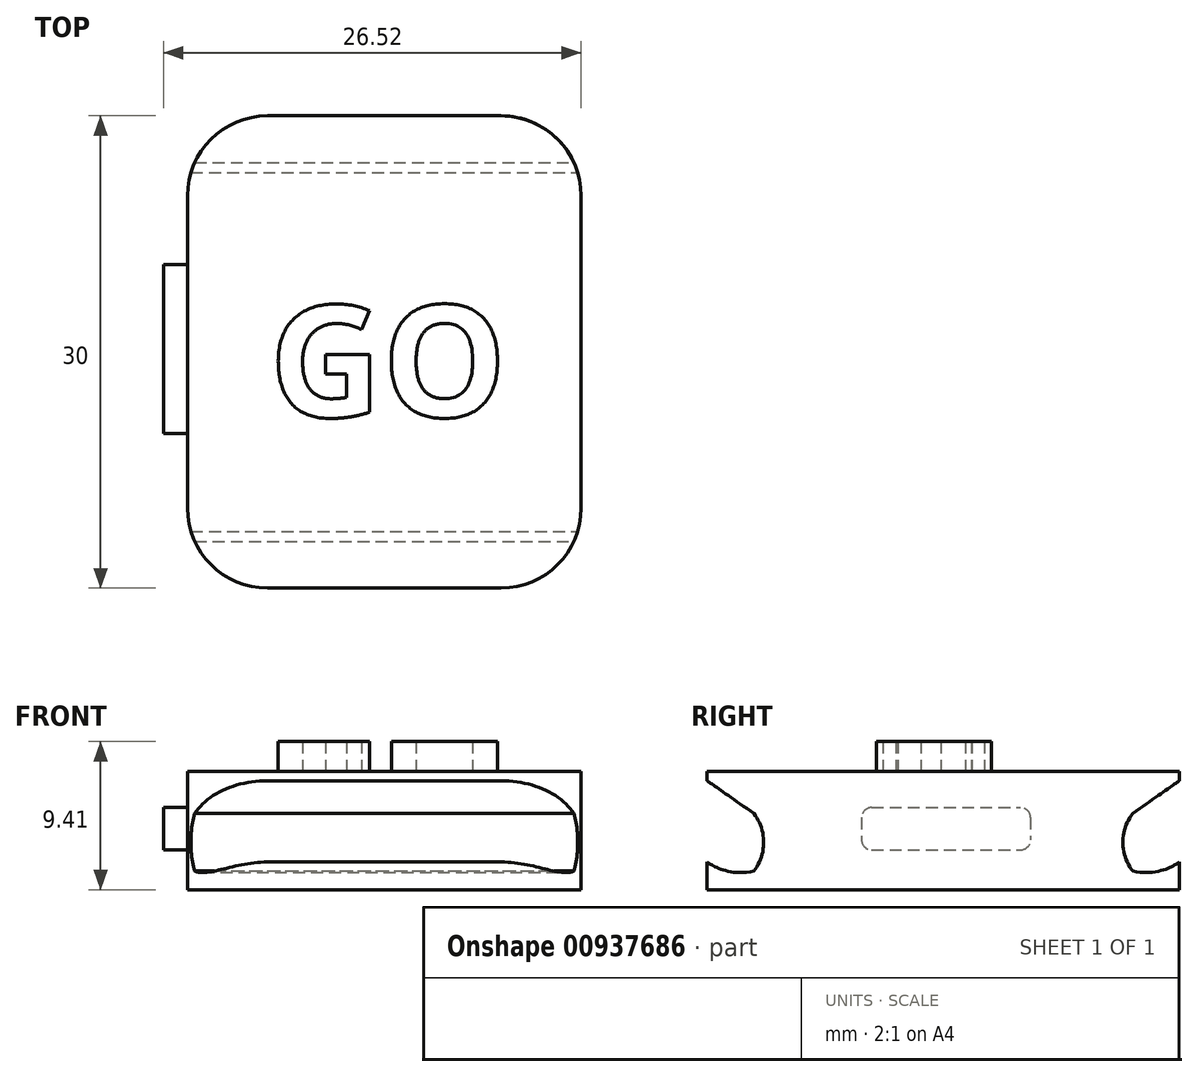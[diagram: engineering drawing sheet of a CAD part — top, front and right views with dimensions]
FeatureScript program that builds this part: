
annotation { "Feature Type Name" : "Feature", "Feature Type Description" : "" }
export const myFeature = defineFeature(function(context is Context, id is Id, definition is map)
    precondition{}
    {
        {
            var Q0;
            Q0=qCreatedBy(makeId("Top.planeOp"),FACE);
            var sketch = newSketch(context, id + "F0", { "sketchPlane" : qUnion([Q0])});
            skLineSegment(sketch, "E0.bottom", {"start": v(0, 0) * mm, "end": v(25, 0) * mm});
            skLineSegment(sketch, "E0.top", {"start": v(0, 30) * mm, "end": v(25, 30) * mm});
            skLineSegment(sketch, "E0.left", {"start": v(0, 0) * mm, "end": v(0, 30) * mm});
            skLineSegment(sketch, "E0.right", {"start": v(25, 0) * mm, "end": v(25, 30) * mm});
            skSolve(sketch);
        }
        {
            var Q0;
            Q0=makeQuery(id+"F0.imprint","IMPRINT",FACE,{"disambiguationData":[TD([[makeQuery(id+"F0.imprint","IMPRINT",EDGE,{"derivedFrom":sQuery(id+"F0.wireOp",EDGE,"E0.bottom")}),1.0]])]});
            extrude(context, id + "F1", {"entities" : qUnion([Q0]), "depth" : 7.5 * mm, "offsetDistance" : 25.4 * mm});
        }
        {
            var Q0;
            Q0=makeQuery(id+"F1.opExtrude","SWEPT_FACE",FACE,{"disambiguationData":[OSD([sQuery(id+"F0.wireOp",EDGE,"E0.right")])]});
            var sketch = newSketch(context, id + "F2", { "sketchPlane" : qUnion([Q0])});
            skArc(sketch, "E1", {"start": v(0, 1.76) * mm, "mid": v(1.42, 1.16) * mm, "end": v(2.97, 1.19) * mm});
            skArc(sketch, "E2", {"start": v(2.97, 1.19) * mm, "mid": v(3.6, 3.02) * mm, "end": v(2.97, 4.84) * mm});
            skLineSegment(sketch, "E3", {"start": v(2.97, 4.84) * mm, "end": v(0, 6.92) * mm});
            skLineSegment(sketch, "E4", {"start": v(15, 7.5) * mm, "end": v(15, 0) * mm, "construction": true});
            skLineSegment(sketch, "E5.MirrorCS", {"start": v(27.03, 4.84) * mm, "end": v(30, 6.92) * mm});
            skArc(sketch, "E6.MirrorCS", {"start": v(27.03, 1.19) * mm, "mid": v(26.4, 3.02) * mm, "end": v(27.03, 4.84) * mm});
            skArc(sketch, "E7.MirrorCS", {"start": v(30, 1.76) * mm, "mid": v(28.58, 1.16) * mm, "end": v(27.03, 1.19) * mm});
            skLineSegment(sketch, "E8", {"start": v(0, 6.92) * mm, "end": v(0, 1.76) * mm});
            skLineSegment(sketch, "E9", {"start": v(30, 6.92) * mm, "end": v(30, 1.76) * mm});
            skSolve(sketch);
        }
        {
            var Q0;
            Q0 = qSketchRegion(id + "F2", true);
            extrude(context, id + "F3", {"entities" : qUnion([Q0]), "operationType" : NewBodyOperationType.REMOVE, "oppositeDirection" : true, "depth" : 25.4 * mm, "offsetDistance" : 25.4 * mm});
        }
        {
            var Q0;
            {var subQ0=sQuery(id+"F0.wireOp",EDGE,"E0.bottom");var subQ1=sQuery(id+"F0.wireOp",EDGE,"E0.right");Q0=makeQuery(id+"F3.boolean.opBoolean","SPLIT",EDGE,{"disambiguationData":[TD([makeQuery(id+"F3.opExtrude","SWEPT_FACE",FACE,{"disambiguationData":[OSD([sQuery(id+"F2.wireOp",EDGE,"E3")])]})])],"derivedFrom":makeQuery(id+"F1.opExtrude","SWEPT_EDGE",EDGE,{"disambiguationData":[OSD([subQ0,subQ1])]})});}
            var Q1;
            {var subQ0=sQuery(id+"F0.wireOp",EDGE,"E0.bottom");var subQ1=sQuery(id+"F0.wireOp",EDGE,"E0.left");Q1=makeQuery(id+"F3.boolean.opBoolean","SPLIT",EDGE,{"disambiguationData":[TD([makeQuery(id+"F3.opExtrude","SWEPT_FACE",FACE,{"disambiguationData":[OSD([sQuery(id+"F2.wireOp",EDGE,"E3")])]})])],"derivedFrom":makeQuery(id+"F1.opExtrude","SWEPT_EDGE",EDGE,{"disambiguationData":[OSD([subQ0,subQ1])]})});}
            var Q2;
            {var subQ0=sQuery(id+"F0.wireOp",EDGE,"E0.left");var subQ1=sQuery(id+"F0.wireOp",EDGE,"E0.top");Q2=makeQuery(id+"F3.boolean.opBoolean","SPLIT",EDGE,{"disambiguationData":[TD([makeQuery(id+"F3.opExtrude","SWEPT_FACE",FACE,{"disambiguationData":[OSD([sQuery(id+"F2.wireOp",EDGE,"E5.MirrorCS")])]})])],"derivedFrom":makeQuery(id+"F1.opExtrude","SWEPT_EDGE",EDGE,{"disambiguationData":[OSD([subQ1,subQ0])]})});}
            var Q3;
            {var subQ0=sQuery(id+"F0.wireOp",EDGE,"E0.right");var subQ1=sQuery(id+"F0.wireOp",EDGE,"E0.top");Q3=makeQuery(id+"F3.boolean.opBoolean","SPLIT",EDGE,{"disambiguationData":[TD([makeQuery(id+"F3.opExtrude","SWEPT_FACE",FACE,{"disambiguationData":[OSD([sQuery(id+"F2.wireOp",EDGE,"E5.MirrorCS")])]})])],"derivedFrom":makeQuery(id+"F1.opExtrude","SWEPT_EDGE",EDGE,{"disambiguationData":[OSD([subQ1,subQ0])]})});}
            fillet(context, id + "F4", {"entities" : qUnion([Q0, Q1, Q2, Q3]), "radius" : 5.08 * mm, "tangentPropagation" : true, "allowEdgeOverflow" : false});
        }
        {
            var Q0;
            Q0=makeQuery(id+"F1.opExtrude","SWEPT_FACE",FACE,{"disambiguationData":[OSD([sQuery(id+"F0.wireOp",EDGE,"E0.left")])]});
            var sketch = newSketch(context, id + "F5", { "sketchPlane" : qUnion([Q0])});
            skLineSegment(sketch, "E10.bottom", {"start": v(-9.82, 5.22) * mm, "end": v(-20.54, 5.22) * mm});
            skLineSegment(sketch, "E10.top", {"start": v(-9.82, 2.53) * mm, "end": v(-20.54, 2.53) * mm});
            skLineSegment(sketch, "E10.left", {"start": v(-9.82, 5.22) * mm, "end": v(-9.82, 2.53) * mm});
            skLineSegment(sketch, "E10.right", {"start": v(-20.54, 5.22) * mm, "end": v(-20.54, 2.53) * mm});
            skSolve(sketch);
        }
        {
            var Q0;
            Q0 = qSketchRegion(id + "F5", true);
            extrude(context, id + "F6", {"entities" : qUnion([Q0]), "operationType" : NewBodyOperationType.ADD, "depth" : 1.52 * mm, "offsetDistance" : 25.4 * mm});
        }
        {
            var Q0;
            Q0=makeQuery(id+"F6.opExtrude","SWEPT_EDGE",EDGE,{"disambiguationData":[OSD([sQuery(id+"F5.wireOp",EDGE,"E10.bottom"),sQuery(id+"F5.wireOp",EDGE,"E10.left")])]});
            var Q1;
            Q1=makeQuery(id+"F6.opExtrude","SWEPT_EDGE",EDGE,{"disambiguationData":[OSD([sQuery(id+"F5.wireOp",EDGE,"E10.top"),sQuery(id+"F5.wireOp",EDGE,"E10.left")])]});
            var Q2;
            Q2=makeQuery(id+"F6.opExtrude","SWEPT_EDGE",EDGE,{"disambiguationData":[OSD([sQuery(id+"F5.wireOp",EDGE,"E10.bottom"),sQuery(id+"F5.wireOp",EDGE,"E10.right")])]});
            var Q3;
            Q3=makeQuery(id+"F6.opExtrude","SWEPT_EDGE",EDGE,{"disambiguationData":[OSD([sQuery(id+"F5.wireOp",EDGE,"E10.top"),sQuery(id+"F5.wireOp",EDGE,"E10.right")])]});
            fillet(context, id + "F7", {"entities" : qUnion([Q0, Q1, Q2, Q3]), "radius" : 0.64 * mm, "tangentPropagation" : true, "allowEdgeOverflow" : false});
        }
        {
            var Q0;
            Q0=makeQuery(id+"F1.opExtrude","CAP_FACE",FACE,{"disambiguationData":[OSD([sQuery(id+"F0.wireOp",EDGE,"E0.bottom"),sQuery(id+"F0.wireOp",EDGE,"E0.top"),sQuery(id+"F0.wireOp",EDGE,"E0.left"),sQuery(id+"F0.wireOp",EDGE,"E0.right")])],"isStart":false});
            var sketch = newSketch(context, id + "F8", { "sketchPlane" : qUnion([Q0])});
            skText(sketch, "E11", { "text": "GO\n", "fontName": "OpenSans-Bold.ttf"});
            const initialGuessF8  = {"E11": [0.00519, 0.01087, 1, 0, 0.00714]};
            skSetInitialGuess(sketch, initialGuessF8);
            skSolve(sketch);
        }
        {
            var Q0;
            Q0 = qSketchRegion(id + "F8", true);
            extrude(context, id + "F9", {"entities" : qUnion([Q0]), "operationType" : NewBodyOperationType.ADD, "depth" : 1.9 * mm, "offsetDistance" : 25.4 * mm});
        }
    });
